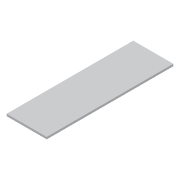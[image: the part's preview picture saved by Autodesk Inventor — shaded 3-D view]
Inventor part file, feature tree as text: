
AUTODESK INVENTOR PART (.ipt)
format: ipt  version: 2016 (Build 200138000, 138)  size: 69,120 bytes
history: native  units: mm
features: extrude x1, plane x1, sketch x1
ambient origin geometry x8: Origin, YZ Plane, XZ Plane, XY Plane, X Axis, Y Axis, Z Axis, Center Point
bodies: Volumenkörper1 (feature_tree)
feature tree (3):
  extrude  "Extrusion1"  Depth=600.0mm
  plane  "Arbeitsebene1"
  sketch  "Skizze1"  dims[d0=190.0mm d1=600.0mm d2=10.0mm d3=0.0mm]
